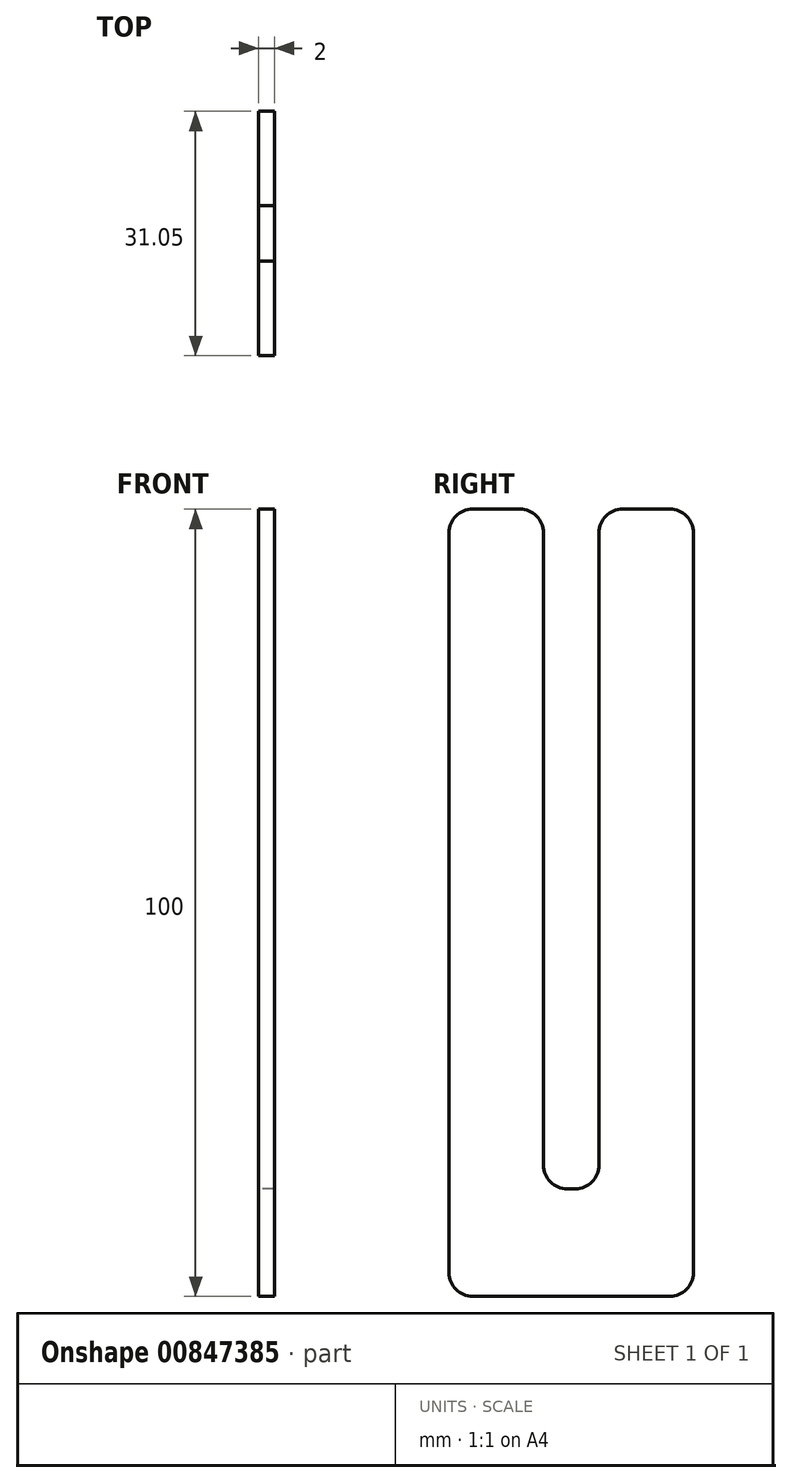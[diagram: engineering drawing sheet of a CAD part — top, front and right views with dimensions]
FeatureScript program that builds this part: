
annotation { "Feature Type Name" : "Feature", "Feature Type Description" : "" }
export const myFeature = defineFeature(function(context is Context, id is Id, definition is map)
    precondition{}
    {
        {
            var Q0;
            Q0=qCreatedBy(makeId("Right.planeOp"),FACE);
            var sketch = newSketch(context, id + "F0", { "sketchPlane" : qUnion([Q0])});
            skLineSegment(sketch, "E0", {"start": v(-19.05, 72.63) * mm, "end": v(-19.05, -21.37) * mm});
            skLineSegment(sketch, "E1", {"start": v(-16.05, -24.37) * mm, "end": v(9, -24.37) * mm});
            skLineSegment(sketch, "E2", {"start": v(12, -21.37) * mm, "end": v(12, 72.63) * mm});
            skLineSegment(sketch, "E3", {"start": v(9, 75.63) * mm, "end": v(3, 75.63) * mm});
            skLineSegment(sketch, "E4", {"start": v(0, 72.63) * mm, "end": v(0, -7.7) * mm});
            skLineSegment(sketch, "E5", {"start": v(-3, -10.7) * mm, "end": v(-4.05, -10.7) * mm});
            skLineSegment(sketch, "E6", {"start": v(-7.05, -7.7) * mm, "end": v(-7.05, 72.63) * mm});
            skLineSegment(sketch, "E7", {"start": v(-10.05, 75.63) * mm, "end": v(-16.05, 75.63) * mm});
            skPoint(sketch, "E8.visualSharp", {"position": v(-7.05, -10.7) * mm});
            skArc(sketch, "E8.filletArc", {"start": v(-7.05, -7.7) * mm, "mid": v(-6.17, -9.83) * mm, "end": v(-4.05, -10.7) * mm});
            skPoint(sketch, "E9.visualSharp", {"position": v(0, -10.7) * mm});
            skArc(sketch, "E9.filletArc", {"start": v(-3, -10.7) * mm, "mid": v(-0.88, -9.83) * mm, "end": v(0, -7.7) * mm});
            skPoint(sketch, "E10.visualSharp", {"position": v(0, 75.63) * mm});
            skArc(sketch, "E10.filletArc", {"start": v(3, 75.63) * mm, "mid": v(0.88, 74.76) * mm, "end": v(0, 72.63) * mm});
            skPoint(sketch, "E11.visualSharp", {"position": v(12, 75.63) * mm});
            skArc(sketch, "E11.filletArc", {"start": v(12, 72.63) * mm, "mid": v(11.12, 74.76) * mm, "end": v(9, 75.63) * mm});
            skPoint(sketch, "E12.visualSharp", {"position": v(12, -24.37) * mm});
            skArc(sketch, "E12.filletArc", {"start": v(9, -24.37) * mm, "mid": v(11.12, -23.49) * mm, "end": v(12, -21.37) * mm});
            skPoint(sketch, "E13.visualSharp", {"position": v(-19.05, -24.37) * mm});
            skArc(sketch, "E13.filletArc", {"start": v(-19.05, -21.37) * mm, "mid": v(-18.17, -23.49) * mm, "end": v(-16.05, -24.37) * mm});
            skPoint(sketch, "E14.visualSharp", {"position": v(-19.05, 75.63) * mm});
            skArc(sketch, "E14.filletArc", {"start": v(-16.05, 75.63) * mm, "mid": v(-18.17, 74.76) * mm, "end": v(-19.05, 72.63) * mm});
            skPoint(sketch, "E15.visualSharp", {"position": v(-7.05, 75.63) * mm});
            skArc(sketch, "E15.filletArc", {"start": v(-7.05, 72.63) * mm, "mid": v(-7.93, 74.76) * mm, "end": v(-10.05, 75.63) * mm});
            skSolve(sketch);
        }
        {
            var Q0;
            Q0 = qSketchRegion(id + "F0", true);
            extrude(context, id + "F1", {"entities" : qUnion([Q0]), "depth" : 2 * mm, "offsetDistance" : 25 * mm});
        }
    });
